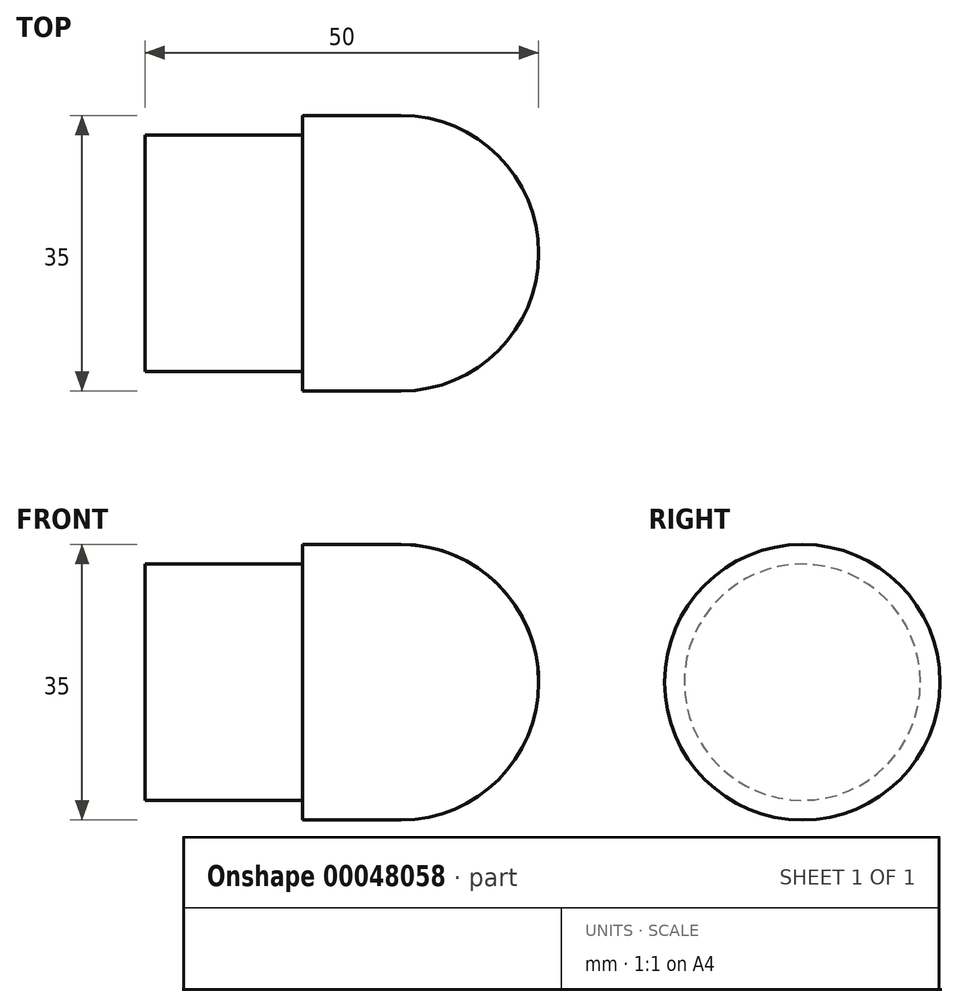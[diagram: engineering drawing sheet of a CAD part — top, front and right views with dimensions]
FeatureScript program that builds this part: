
annotation { "Feature Type Name" : "Feature", "Feature Type Description" : "" }
export const myFeature = defineFeature(function(context is Context, id is Id, definition is map)
    precondition{}
    {
        {
            var Q0;
            Q0=qCreatedBy(makeId("Front.planeOp"),FACE);
            var sketch = newSketch(context, id + "F0", { "sketchPlane" : qUnion([Q0])});
            skLineSegment(sketch, "E0.bottom", {"start": v(0, 0) * mm, "end": v(20, 0) * mm});
            skLineSegment(sketch, "E0.top", {"start": v(0, 30) * mm, "end": v(20, 30) * mm});
            skLineSegment(sketch, "E0.left", {"start": v(0, 0) * mm, "end": v(0, 30) * mm});
            skLineSegment(sketch, "E0.right", {"start": v(20, 0) * mm, "end": v(20, 30) * mm});
            skLineSegment(sketch, "E1.bottom", {"start": v(20, -2.5) * mm, "end": v(32.5, -2.5) * mm});
            skLineSegment(sketch, "E1.top", {"start": v(20, 32.5) * mm, "end": v(32.5, 32.5) * mm});
            skLineSegment(sketch, "E1.left", {"start": v(20, -2.5) * mm, "end": v(20, 32.5) * mm});
            skLineSegment(sketch, "E1.right", {"start": v(32.5, -2.5) * mm, "end": v(32.5, 32.5) * mm});
            skLineSegment(sketch, "E2", {"start": v(0, 15) * mm, "end": v(32.5, 15) * mm});
            skArc(sketch, "E3", {"start": v(32.5, -2.5) * mm, "mid": v(50, 15) * mm, "end": v(32.5, 32.5) * mm});
            skLineSegment(sketch, "E4", {"start": v(32.5, 15) * mm, "end": v(50, 15) * mm});
            skSolve(sketch);
        }
        {
            var Q0;
            {var subQ5=sQuery(id+"F0.wireOp",EDGE,"E0.top");Q0=makeQuery(id+"F0.imprint","IMPRINT",FACE,{"disambiguationData":[TD([[makeQuery(id+"F0.imprint","IMPRINT",EDGE,{"derivedFrom":subQ5}),-1.0]])]});}
            var Q1;
            {var subQ5=sQuery(id+"F0.wireOp",EDGE,"E1.top");Q1=makeQuery(id+"F0.imprint","IMPRINT",FACE,{"disambiguationData":[TD([[makeQuery(id+"F0.imprint","IMPRINT",EDGE,{"derivedFrom":subQ5}),-1.0]])]});}
            var Q2;
            {var subQ0=sQuery(id+"F0.wireOp",EDGE,"E4");Q2=makeQuery(id+"F0.imprint","IMPRINT",FACE,{"disambiguationData":[TD([[makeQuery(id+"F0.imprint","IMPRINT",EDGE,{"derivedFrom":subQ0}),1.0]])]});}
            var Q3;
            Q3=sQuery(id+"F0.wireOp",EDGE,"E2");
            revolve(context, id + "F1", {"entities" : qUnion([Q0, Q1, Q2]), "axis" : qUnion([Q3]), "revolveType" : RevolveType.FULL});
        }
    });
